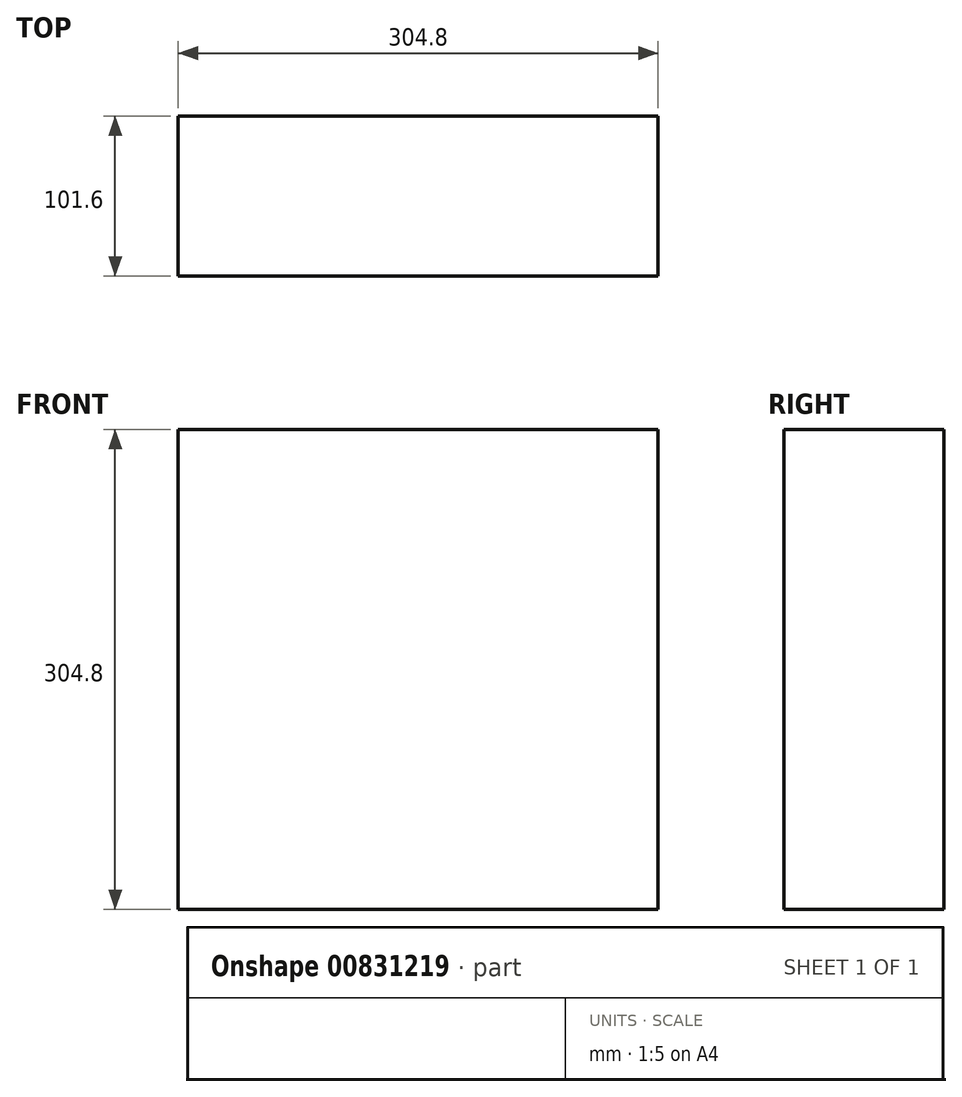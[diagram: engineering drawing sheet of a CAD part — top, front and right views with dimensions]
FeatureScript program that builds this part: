
annotation { "Feature Type Name" : "Feature", "Feature Type Description" : "" }
export const myFeature = defineFeature(function(context is Context, id is Id, definition is map)
    precondition{}
    {
        {
            var Q0;
            Q0=qCreatedBy(makeId("Front.planeOp"),FACE);
            var sketch = newSketch(context, id + "F0", { "sketchPlane" : qUnion([Q0])});
            skLineSegment(sketch, "E0.bottom", {"start": v(152.4, 152.4) * mm, "end": v(-152.4, 152.4) * mm});
            skLineSegment(sketch, "E0.top", {"start": v(152.4, -152.4) * mm, "end": v(-152.4, -152.4) * mm});
            skLineSegment(sketch, "E0.left", {"start": v(152.4, 152.4) * mm, "end": v(152.4, -152.4) * mm});
            skLineSegment(sketch, "E0.right", {"start": v(-152.4, 152.4) * mm, "end": v(-152.4, -152.4) * mm});
            skPoint(sketch, "E0.middle", {"position": v(0, 0) * mm});
            skSolve(sketch);
        }
        {
            var Q0;
            Q0=qSketchRegion(id+"F0",true);
            extrude(context, id + "F1", {"entities" : qUnion([Q0]), "depth" : 101.6 * mm, "offsetDistance" : 25.4 * mm});
        }
    });
